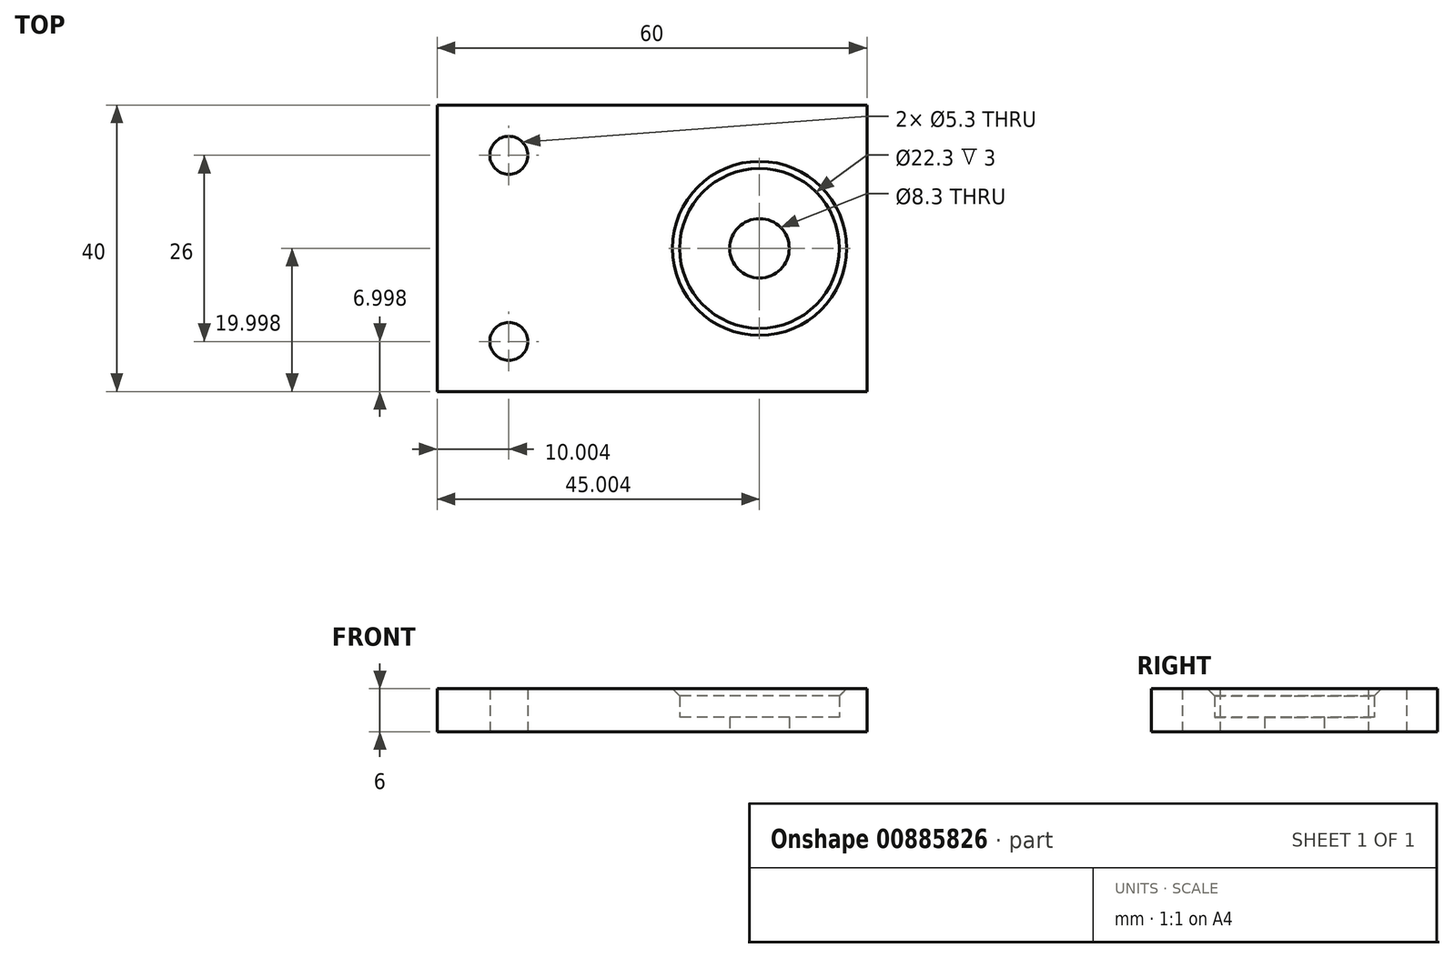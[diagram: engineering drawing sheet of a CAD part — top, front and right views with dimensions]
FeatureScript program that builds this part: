
annotation { "Feature Type Name" : "Feature", "Feature Type Description" : "" }
export const myFeature = defineFeature(function(context is Context, id is Id, definition is map)
    precondition{}
    {
        {
            var Q0;
            Q0=qCreatedBy(makeId("Top.planeOp"),FACE);
            var sketch = newSketch(context, id + "F0", { "sketchPlane" : qUnion([Q0])});
            skLineSegment(sketch, "E0.bottom", {"start": v(-91.93, 42.42) * mm, "end": v(-71.93, 42.42) * mm});
            skLineSegment(sketch, "E0.top", {"start": v(-91.93, 2.42) * mm, "end": v(-71.93, 2.42) * mm});
            skLineSegment(sketch, "E0.left", {"start": v(-91.93, 42.42) * mm, "end": v(-91.93, 2.42) * mm});
            skLineSegment(sketch, "E0.right", {"start": v(-71.93, 42.42) * mm, "end": v(-71.93, 2.42) * mm});
            skCircle(sketch, "E1", {"center": v(-81.93, 35.42) * mm, "radius": 2.65 * mm});
            skCircle(sketch, "E2", {"center": v(-81.93, 9.42) * mm, "radius": 2.65 * mm});
            skPoint(sketch, "E3", {"position": v(-71.93, 42.42) * mm});
            skPoint(sketch, "E4", {"position": v(-71.93, 2.42) * mm});
            skLineSegment(sketch, "E5.bottom", {"start": v(-71.93, 42.42) * mm, "end": v(-31.93, 42.42) * mm});
            skLineSegment(sketch, "E5.top", {"start": v(-71.93, 2.42) * mm, "end": v(-31.93, 2.42) * mm});
            skLineSegment(sketch, "E5.right", {"start": v(-31.93, 42.42) * mm, "end": v(-31.93, 2.42) * mm});
            skCircle(sketch, "E6", {"center": v(-46.93, 22.42) * mm, "radius": 4.15 * mm});
            skCircle(sketch, "E7", {"center": v(-46.93, 22.42) * mm, "radius": 11.15 * mm});
            skSolve(sketch);
        }
        {
            var Q0;
            Q0=makeQuery(id+"F0.imprint","IMPRINT",FACE,{"disambiguationData":[TD([[makeQuery(id+"F0.imprint","IMPRINT",EDGE,{"derivedFrom":sQuery(id+"F0.wireOp",EDGE,"E5.bottom")}),-1.0]])]});
            var Q1;
            Q1=makeQuery(id+"F0.imprint","IMPRINT",FACE,{"disambiguationData":[TD([[makeQuery(id+"F0.imprint","IMPRINT",EDGE,{"derivedFrom":sQuery(id+"F0.wireOp",EDGE,"E0.bottom")}),-1.0]])]});
            extrude(context, id + "F1", {"entities" : qUnion([Q0, Q1]), "depth" : 6 * mm});
        }
        {
            var Q0;
            Q0=makeQuery(id+"F0.imprint","IMPRINT",FACE,{"disambiguationData":[TD([[makeQuery(id+"F0.imprint","IMPRINT",EDGE,{"derivedFrom":sQuery(id+"F0.wireOp",EDGE,"E6")}),-1.0]])]});
            extrude(context, id + "F2", {"entities" : qUnion([Q0]), "operationType" : NewBodyOperationType.ADD, "depth" : 2 * mm});
        }
        {
            var Q0;
            Q0=makeQuery(id+"F1.opExtrude","CAP_EDGE",EDGE,{"disambiguationData":[OSD([sQuery(id+"F0.wireOp",EDGE,"E7")])],"isStart":false});
            chamfer(context, id + "F3", {"entities" : qUnion([Q0]), "width" : 1 * mm, "tangentPropagation" : true});
        }
    });
